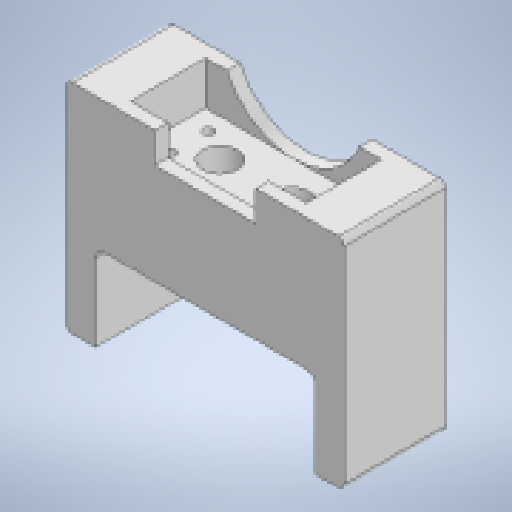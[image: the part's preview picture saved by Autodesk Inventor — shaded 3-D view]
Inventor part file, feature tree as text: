
AUTODESK INVENTOR PART (.ipt)
format: ipt  version: 2023 (Build 270158000, 158)  size: 230,400 bytes
history: native  units: in
note: dims shown in document units (in); Inventor stores cm internally (conversion verified against a paired STEP export)
features: extrude x8, sketch x7, fillet x2
ambient origin geometry x8: Origin, YZ Plane, XZ Plane, XY Plane, X Axis, Y Axis, Z Axis, Center Point
bodies: Solid1 (feature_tree)
feature tree (17):
  sketch  "Sketch1"  dims[d0=0.9843in d1=2.3622in]
  extrude  "Extrusion1"  Depth=0.9843in
  extrude  "Extrusion2"  Depth=0.0197in
  extrude  "Extrusion3"  Depth=0.0197in
  extrude  "Extrusion4"  Depth=1.811in
  extrude  "Extrusion5"  Depth=4.1811in
  extrude  "Extrusion6"  Depth=0.3937in TaperAngle=0.0deg
  fillet  "Fillet1"  Radius=1.5118in
  fillet  "Fillet2"  Radius=0.3937in
  extrude  "Extrusion7"  Depth=3.0in
  extrude  "Extrusion8"  Depth=0.125in
  sketch  "Sketch2"  dims[d2=0.0197in d3=0.0197in]
  sketch  "Sketch3"  dims[d4=0.0197in d5=0.0197in]
  sketch  "Sketch4"  dims[d6=0.1417in d7=1.811in]
  sketch  "Sketch5"  dims[d8=0.5118in d9=4.1811in]
  sketch  "Sketch6"  dims[d10=1.378in d11=0.3937in d12=0.0in d13=1.5118in d14=0.0in]
  sketch  "Sketch7"  dims[d15=0.3937in d16=0.1969in d17=0.0in d18=0.0in d19=0.3937in d20=1.1969in d21=0.0in d22=0.0in d23=3.0in d24=0.125in d25=0.7874in d26=1.1811in d27=0.3937in d28=0.0in d29=0.2362in d30=0.9843in d31=0.3937in d32=0.0in d34=0.4724in d35=0.3937in d36=0.0in d37=0.0787in d38=0.0787in d39=1.374in d40=1.378in d41=2.0812in d42=0.0in d44=0.9843in d45=0.3937in d46=0.3937in d47=0.0in d49=1.5748in d50=1.5748in d51=0.3937in]
